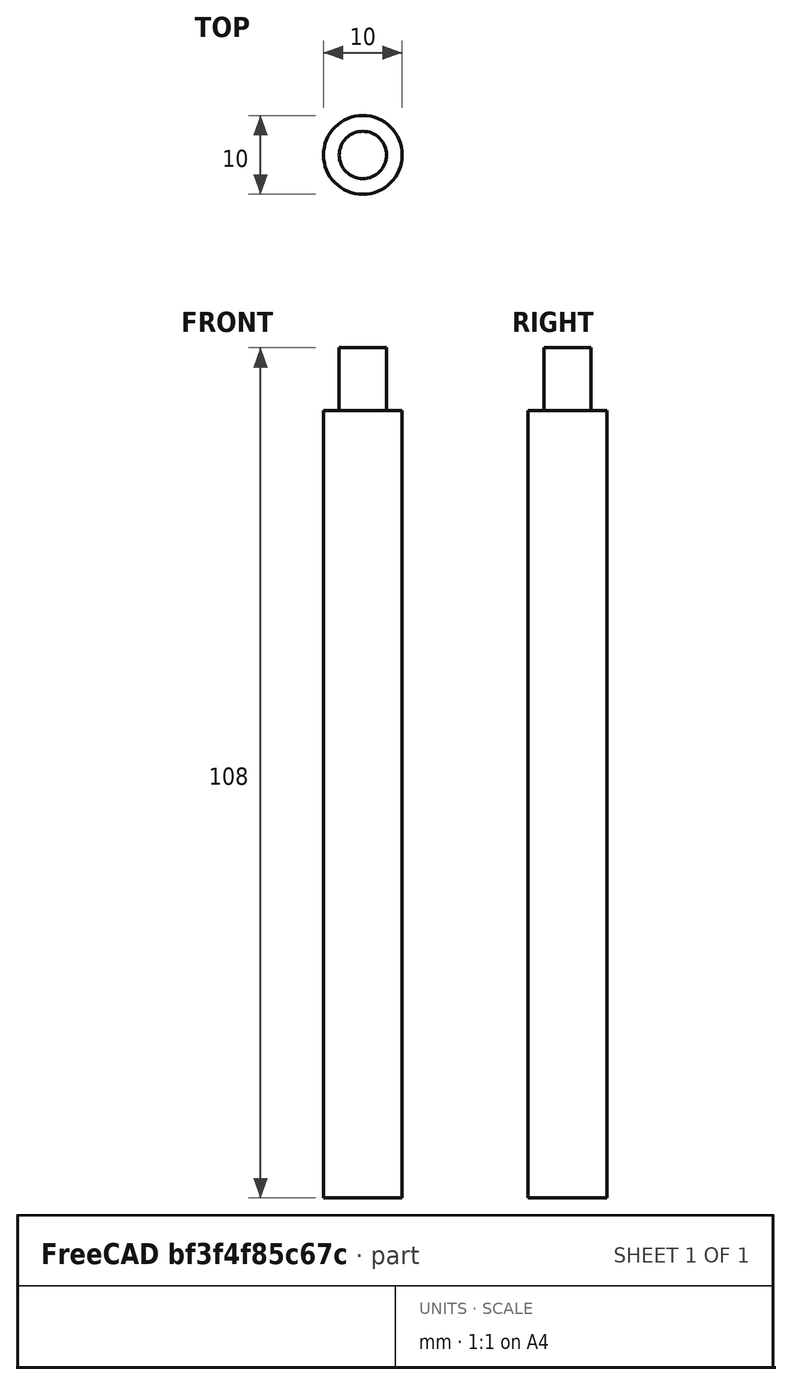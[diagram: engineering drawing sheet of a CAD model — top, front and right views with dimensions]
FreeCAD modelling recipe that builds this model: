
FCSTD DOCUMENT  (FreeCAD 0.18R16146 (Git))
Label: rod
Comment: # 2020-08-04 16:30:36: read from <userpath>/repositories/sussex_neuro/Olfactometer/hardware/mechanics/from_raiser_et_al/rod.ipt
License: All rights reserved
LicenseURL: http://en.wikipedia.org/wiki/All_rights_reserved
objects: Sketcher::SketchObject×4, Part::Extrusion×2, Spreadsheet::Sheet×1, Part::Feature×1
note: 7 computed .brp shape members not serialized (recipe doc carries the construction recipe); baked Part::Feature solids carry a one-line shape summary decoded from their .brp

FEATURE [Spreadsheet::Sheet] Parameters
  cells = A1=Parameter; B1=Value; C1=Fromula; D1=Tolerance; E1=Comment; A2=d0; B2(d0_)=10; C2=10mm; D2=NOMINAL; A3=d1; B3(d1_)=100; C3=100mm; D3=NOMINAL; A4=d10; B4(d10_)=45; C4=45°; D4=NOMINAL; A5=d2; B5(d2_)=0; C5=0°; D5=NOMINAL; A6=d3; B6(d3_)=6.000000000000001; C6=6mm; D6=NOMINAL; A7=d4; B7(d4_)=8; C7=8mm; D7=NOMINAL; A8=d5; B8(d5_)=0; C8=0°; D8=NOMINAL; A9=d6; B9(d6_)=10; C9=10mm; D9=NOMINAL; A10=d7; B10(d7_)=0; C10=0mm; D10=NOMINAL; A11=d8; B11(d8_)=1; C11=1mm; D11=NOMINAL; A12=d9; B12(d9_)=2; C12=2mm; D12=NOMINAL
FEATURE [Sketcher::SketchObject] Sketch1
  sketch-geometry (1):
    g0: Circle CenterX=0 CenterY=0 CenterZ=0 NormalX=0 NormalY=0 NormalZ=1 AngleXU=0 Radius=5
  constraints (1):
    c: Radius(g0) = 5  'd0'
FEATURE [Sketcher::SketchObject] Sketch1_bp
  sketch-geometry (1):
    g0: Circle CenterX=0 CenterY=0 CenterZ=0 NormalX=0 NormalY=0 NormalZ=1 AngleXU=0 Radius=5
FEATURE [Part::Extrusion] Extrusion1
  Base = -> Sketch1_bp
  Dir = (0,0,1)
  DirMode = 0
  FaceMakerClass = Part::FaceMakerBullseye
  LengthFwd = 100
  LengthRev = 0
  Solid = true
  Symmetric = false
  expr: LengthFwd = Parameters.d1_
  expr: TaperAngle = Parameters.d2_
FEATURE [Sketcher::SketchObject] Sketch3
  Placement = pos=(0,0,100) rot=(0,0,1;0rad)
  sketch-geometry (2):
    g0: Circle [constr] CenterX=0 CenterY=0 CenterZ=0 NormalX=0 NormalY=0 NormalZ=1 AngleXU=0 Radius=5
    g1: Circle CenterX=0 CenterY=0 CenterZ=0 NormalX=0 NormalY=0 NormalZ=1 AngleXU=0 Radius=3
  constraints (1):
    c: Radius(g1) = 3  'd3'
FEATURE [Sketcher::SketchObject] Sketch3_bp
  Placement = pos=(0,0,100) rot=(0,0,1;0rad)
  sketch-geometry (1):
    g0: Circle CenterX=0 CenterY=0 CenterZ=0 NormalX=0 NormalY=0 NormalZ=1 AngleXU=0 Radius=3
FEATURE [Part::Extrusion] Extrusion2
  Base = -> Sketch3_bp
  Dir = (0,0,1)
  DirMode = 0
  FaceMakerClass = Part::FaceMakerBullseye
  LengthFwd = 8
  LengthRev = 0
  Solid = true
  Symmetric = false
  expr: LengthFwd = Parameters.d4_
  expr: TaperAngle = Parameters.d5_
FEATURE [Part::Feature] Thread1
  shape: bbox 6 x 6 x 8 mm, 2 faces, 0 solids (baked)
